# Revit family: KINGSLEY Single Towel Rail
name_source: partatom
category: Generic Models
units: mm (PartAtom-declared; Revit-internal decimal feet)

## family parameters
Always vertical = Yes
Can host rebar = No
Cut with Voids When Loaded = No
Maintain Annotation Orientation = No
OmniClass Number = 23.31.25.25
Part Type = Normal
Room Calculation Point = No
Round Connector Dimension = Use Diameter
Shared = No
Work Plane-Based = No

## types (1)
- KINGSLEY SIngle Towel Rail
    Default Elevation = 0 mm  [stored 0 ft]
    Description = KINGSLEY SIngle Towel Rail
    Manufacturer = ABI Interiors PTY LTD
    Model = Brass (1411), Nickel (1412), Chroms AUS/NZ (1413)
    URL = https://www.abiinteriors.com.au
    URL - AUS = https://www.abiinteriors.com.au
    URL - NZ = https://www.abiinteriors.co.nz
    URL - UK = https://www.abiinteriors.co.uk

note: [stored X ft] marks values corroborated as IEEE doubles in the binary element streams (Revit-internal decimal feet)

## geometry (parser evidence)
native form markers: Sweep x3
no freeform markers — native parametric forms only
